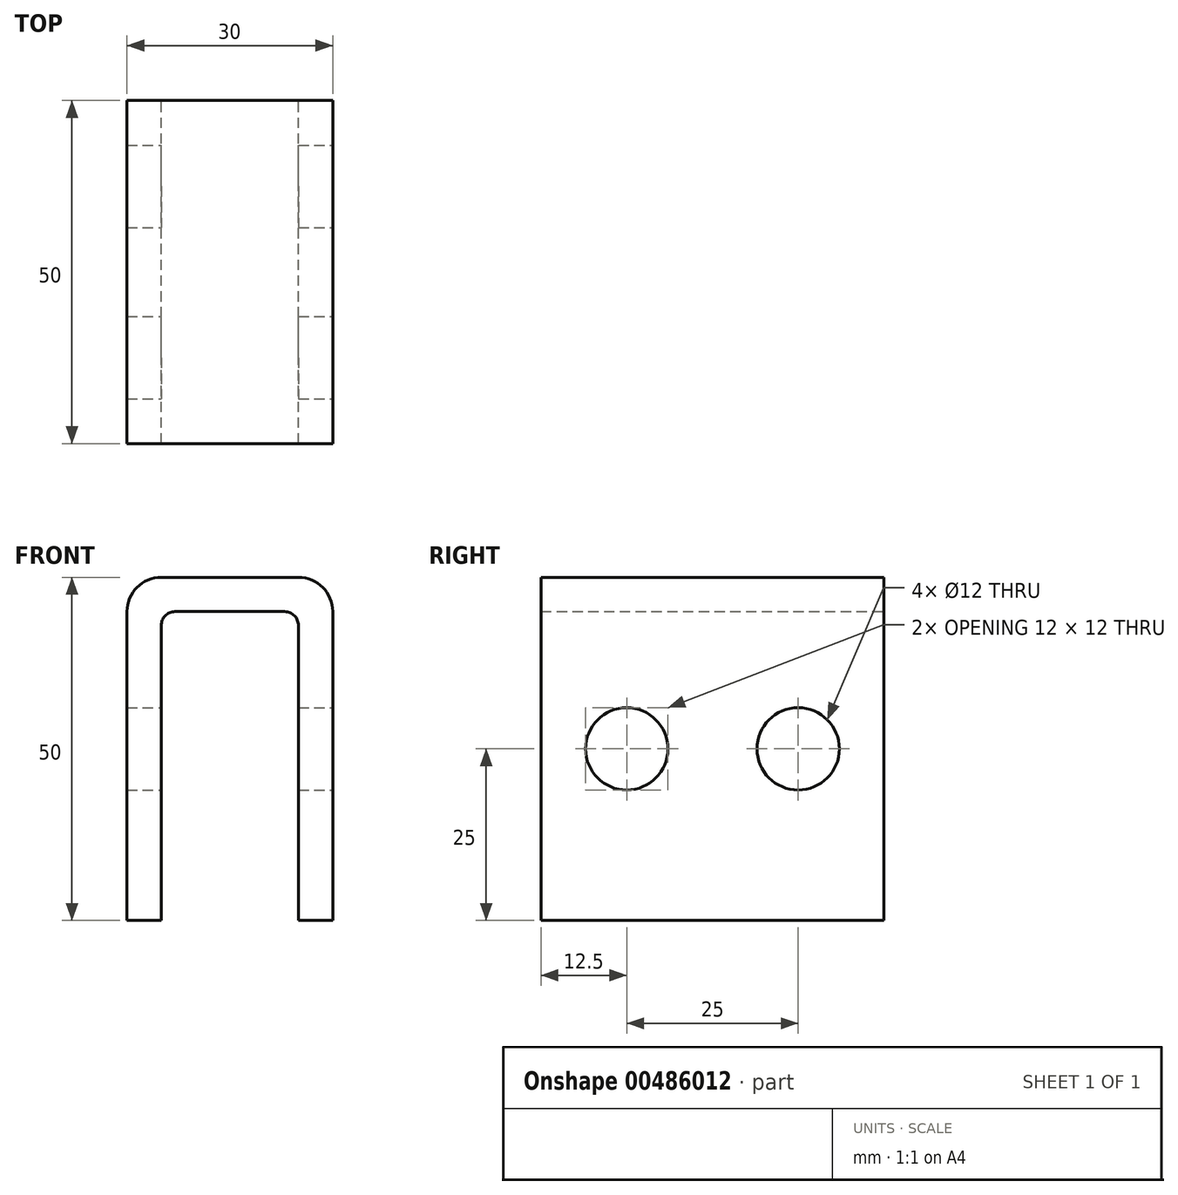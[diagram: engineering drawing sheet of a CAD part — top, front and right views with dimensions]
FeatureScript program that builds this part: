
annotation { "Feature Type Name" : "Feature", "Feature Type Description" : "" }
export const myFeature = defineFeature(function(context is Context, id is Id, definition is map)
    precondition{}
    {
        {
            var Q0;
            Q0=qCreatedBy(makeId("Front.planeOp"),FACE);
            var sketch = newSketch(context, id + "F0", { "sketchPlane" : qUnion([Q0])});
            skLineSegment(sketch, "E0.bottom", {"start": v(15, 25) * mm, "end": v(-15, 25) * mm});
            skLineSegment(sketch, "E0.top", {"start": v(15, -25) * mm, "end": v(10, -25) * mm});
            skLineSegment(sketch, "E0.left", {"start": v(15, 25) * mm, "end": v(15, -25) * mm});
            skLineSegment(sketch, "E0.right", {"start": v(-15, 25) * mm, "end": v(-15, -25) * mm});
            skPoint(sketch, "E0.middle", {"position": v(0, 0) * mm});
            skLineSegment(sketch, "E1.top", {"start": v(-10, 20) * mm, "end": v(10, 20) * mm});
            skLineSegment(sketch, "E1.left", {"start": v(-10, -25) * mm, "end": v(-10, 20) * mm});
            skLineSegment(sketch, "E1.right", {"start": v(10, -25) * mm, "end": v(10, 20) * mm});
            skLineSegment(sketch, "E2.trimOffspring", {"start": v(-10, -25) * mm, "end": v(-15, -25) * mm});
            skSolve(sketch);
        }
        {
            var Q0;
            Q0=makeQuery(id+"F0.imprint","IMPRINT",FACE,{"disambiguationData":[TD([[makeQuery(id+"F0.imprint","IMPRINT",EDGE,{"derivedFrom":sQuery(id+"F0.wireOp",EDGE,"E0.bottom")}),1.0]])]});
            extrude(context, id + "F1", {"entities" : qUnion([Q0]), "depth" : 50 * mm});
        }
        {
            var Q0;
            Q0=makeQuery(id+"F1.opExtrude","SWEPT_FACE",FACE,{"disambiguationData":[OSD([sQuery(id+"F0.wireOp",EDGE,"E0.left")])]});
            var sketch = newSketch(context, id + "F2", { "sketchPlane" : qUnion([Q0])});
            skCircle(sketch, "E3", {"center": v(-37.5, 0) * mm, "radius": 6 * mm});
            skPoint(sketch, "E3.centerSnap0", {"position": v(-50, 0) * mm});
            skCircle(sketch, "E4", {"center": v(-12.5, 0) * mm, "radius": 6 * mm});
            skSolve(sketch);
        }
        {
            var Q0;
            Q0 = qSketchRegion(id + "F2", true);
            var Q1;
            Q1=makeQuery(id+"F1.opExtrude","SWEPT_FACE",FACE,{"disambiguationData":[OSD([sQuery(id+"F0.wireOp",EDGE,"E0.right")])]});
            extrude(context, id + "F3", {"entities" : qUnion([Q0]), "operationType" : NewBodyOperationType.REMOVE, "endBound" : BoundingType.UP_TO_SURFACE, "oppositeDirection" : true, "endBoundEntityFace" : qUnion([Q1]), "depth" : 25 * mm});
        }
        {
            var Q0;
            Q0=makeQuery(id+"F1.opExtrude","SWEPT_EDGE",EDGE,{"disambiguationData":[OSD([sQuery(id+"F0.wireOp",EDGE,"E1.top"),sQuery(id+"F0.wireOp",EDGE,"E1.left")])]});
            var Q1;
            Q1=makeQuery(id+"F1.opExtrude","SWEPT_EDGE",EDGE,{"disambiguationData":[OSD([sQuery(id+"F0.wireOp",EDGE,"E1.top"),sQuery(id+"F0.wireOp",EDGE,"E1.right")])]});
            fillet(context, id + "F4", {"entities" : qUnion([Q0, Q1]), "radius" : 2 * mm, "tangentPropagation" : true, "allowEdgeOverflow" : false});
        }
        {
            var Q0;
            Q0=makeQuery(id+"F1.opExtrude","SWEPT_EDGE",EDGE,{"disambiguationData":[OSD([sQuery(id+"F0.wireOp",EDGE,"E0.bottom"),sQuery(id+"F0.wireOp",EDGE,"E0.left")])]});
            var Q1;
            Q1=makeQuery(id+"F1.opExtrude","SWEPT_EDGE",EDGE,{"disambiguationData":[OSD([sQuery(id+"F0.wireOp",EDGE,"E0.bottom"),sQuery(id+"F0.wireOp",EDGE,"E0.right")])]});
            fillet(context, id + "F5", {"entities" : qUnion([Q0, Q1]), "radius" : 5 * mm, "tangentPropagation" : true, "allowEdgeOverflow" : false});
        }
    });
